# Revit family: WH1182
name_source: partatom
category: Mechanical Equipment
revit_build: Autodesk Revit MEP 2016 (Build: 20150220_1215(x64)
units: mm (PartAtom-declared; Revit-internal decimal feet)

## family parameters
Cut with Voids When Loaded = No
Host = Face
OmniClass Number = 23.65.70.11.11
OmniClass Title = Fixtures for Liquids
Part Type = Normal
Room Calculation Point = No
Round Connector Dimension = Use Diameter
Shared = Yes

## types (1)
- WH1182
    Amperage = 0
    CW Connection = No
    Default Elevation = 48 "
    Description = Ligature Resistant Vanity Shelf
    HW Connection = No
    Manufacturer = WHITEHALL
    Material = Stainless Steel
    Model = WH1182
    OVERALL DEPTH = 3
    OVERALL SIZE HEIGHT = 18.5
    OVERALL SIZE WIDTH = 12
    Revised Date = 07/23/19
    Tempered Water Connection = No
    URL = https://www.acorneng.com
    Vent Connection = No
    Voltage = 0
    WH1182 - Ligature Resistant Vanity Shelf = Yes
    Waste Connection = No

## geometry (parser evidence)
native form markers: Sweep x3
no freeform markers — native parametric forms only
